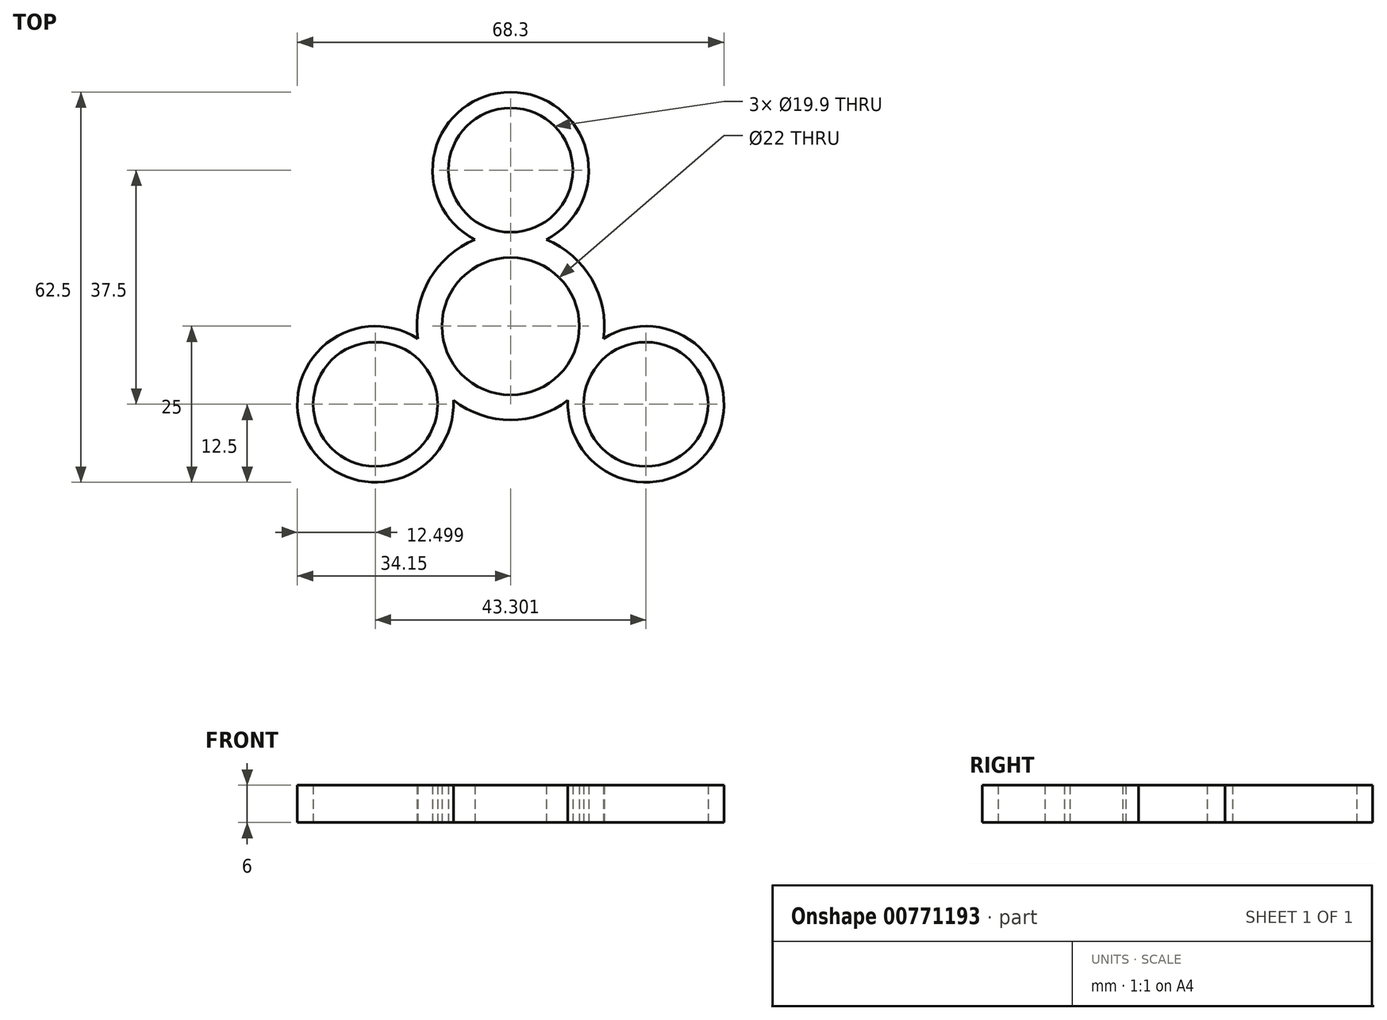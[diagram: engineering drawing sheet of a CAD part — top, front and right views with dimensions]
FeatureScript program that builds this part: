
annotation { "Feature Type Name" : "Feature", "Feature Type Description" : "" }
export const myFeature = defineFeature(function(context is Context, id is Id, definition is map)
    precondition{}
    {
        {
            var Q0;
            Q0=qCreatedBy(makeId("Top.planeOp"),FACE);
            var sketch = newSketch(context, id + "F0", { "sketchPlane" : qUnion([Q0])});
            skCircle(sketch, "E0", {"center": v(0, 0) * mm, "radius": 11 * mm});
            skArc(sketch, "E1", {"start": v(14.87, -2) * mm, "mid": v(13, 7.5) * mm, "end": v(5.7, 13.87) * mm});
            skLineSegment(sketch, "E2", {"start": v(0, 0) * mm, "end": v(0, 15.05) * mm});
            skCircle(sketch, "E3", {"center": v(0, 25) * mm, "radius": 9.95 * mm});
            skArc(sketch, "E4", {"start": v(5.7, 13.88) * mm, "mid": v(0, 37.5) * mm, "end": v(-5.7, 13.88) * mm});
            skCircle(sketch, "E5.1.0", {"center": v(-21.65, -12.5) * mm, "radius": 9.95 * mm});
            skArc(sketch, "E5.1.1", {"start": v(-14.87, -2) * mm, "mid": v(-32.48, -18.75) * mm, "end": v(-9.17, -11.87) * mm});
            skCircle(sketch, "E5.2.0", {"center": v(21.65, -12.5) * mm, "radius": 9.95 * mm});
            skArc(sketch, "E5.2.1", {"start": v(9.17, -11.87) * mm, "mid": v(32.48, -18.75) * mm, "end": v(14.87, -2) * mm});
            skArc(sketch, "E6.trimOffspring", {"start": v(-5.7, 13.87) * mm, "mid": v(-13, 7.5) * mm, "end": v(-14.87, -2) * mm});
            skArc(sketch, "E7.trimOffspring", {"start": v(-9.17, -11.87) * mm, "mid": v(0, -15) * mm, "end": v(9.17, -11.87) * mm});
            skSolve(sketch);
        }
        {
            var Q0;
            Q0 = qSketchRegion(id + "F0", true);
            extrude(context, id + "F1", {"entities" : qUnion([Q0]), "depth" : 6 * mm, "offsetDistance" : 25 * mm});
        }
    });
